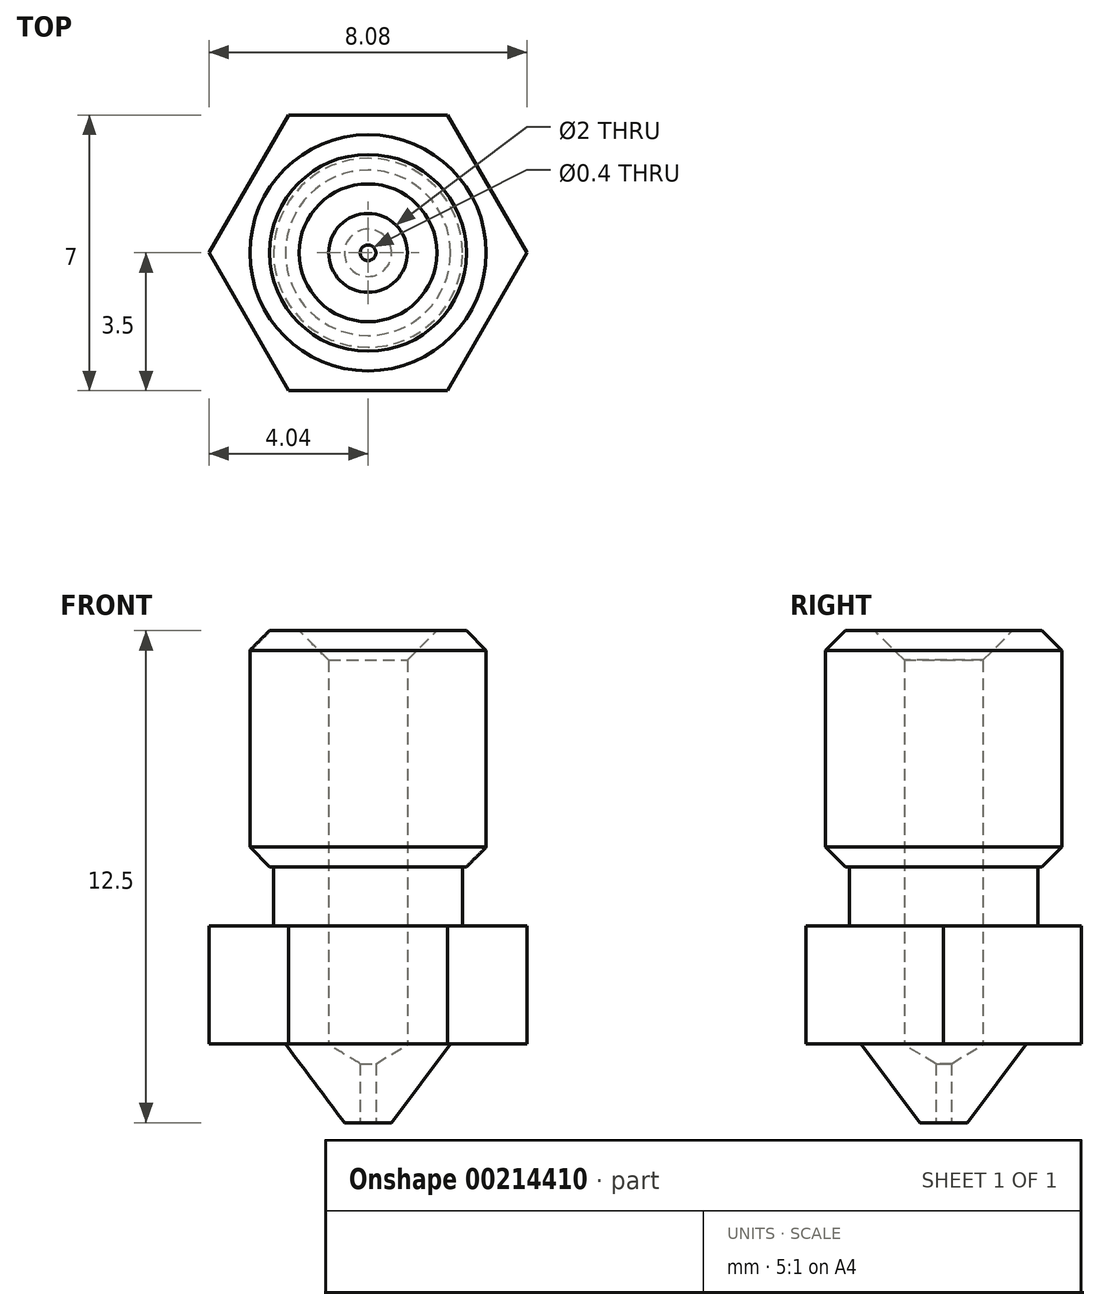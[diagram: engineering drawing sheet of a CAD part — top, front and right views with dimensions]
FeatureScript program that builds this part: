
annotation { "Feature Type Name" : "Feature", "Feature Type Description" : "" }
export const myFeature = defineFeature(function(context is Context, id is Id, definition is map)
    precondition{}
    {
        {
            var Q0;
            Q0=qCreatedBy(makeId("Front.planeOp"),FACE);
            var sketch = newSketch(context, id + "F0", { "sketchPlane" : qUnion([Q0])});
            skLineSegment(sketch, "E0", {"start": v(0, 0) * mm, "end": v(0, 12.5) * mm, "construction": true});
            skLineSegment(sketch, "E1", {"start": v(0.2, 0) * mm, "end": v(0.2, 1.5) * mm});
            skLineSegment(sketch, "E2", {"start": v(0.2, 0) * mm, "end": v(0.6, 0) * mm});
            skLineSegment(sketch, "E3", {"start": v(0.6, 0) * mm, "end": v(2.1, 2) * mm});
            skLineSegment(sketch, "E4", {"start": v(2.1, 2) * mm, "end": v(4.2, 2) * mm});
            skLineSegment(sketch, "E5", {"start": v(4.2, 2) * mm, "end": v(4.2, 5) * mm});
            skLineSegment(sketch, "E6", {"start": v(1, 12.5) * mm, "end": v(1, 1.98) * mm});
            skLineSegment(sketch, "E7", {"start": v(1, 1.98) * mm, "end": v(0.2, 1.5) * mm});
            skLineSegment(sketch, "E8", {"start": v(1, 12.5) * mm, "end": v(3, 12.5) * mm});
            skLineSegment(sketch, "E9", {"start": v(3, 12.5) * mm, "end": v(3, 6.5) * mm});
            skLineSegment(sketch, "E10", {"start": v(3, 6.5) * mm, "end": v(2.4, 6.5) * mm});
            skLineSegment(sketch, "E11", {"start": v(2.4, 6.5) * mm, "end": v(2.4, 5) * mm});
            skLineSegment(sketch, "E12", {"start": v(2.4, 5) * mm, "end": v(4.2, 5) * mm});
            skSolve(sketch);
        }
        {
            var Q0;
            Q0 = qSketchRegion(id + "F0", true);
            var Q1;
            Q1=sQuery(id+"F0.wireOp",EDGE,"E0");
            revolve(context, id + "F1", {"entities" : qUnion([Q0]), "axis" : qUnion([Q1]), "revolveType" : RevolveType.FULL});
        }
        {
            var Q0;
            Q0=makeQuery(id+"F1.opRevolve","SWEPT_EDGE",EDGE,{"disambiguationData":[OSD([sQuery(id+"F0.wireOp",EDGE,"E9"),sQuery(id+"F0.wireOp",EDGE,"E10")])]});
            var Q1;
            Q1=makeQuery(id+"F1.opRevolve","SWEPT_EDGE",EDGE,{"disambiguationData":[OSD([sQuery(id+"F0.wireOp",EDGE,"E8"),sQuery(id+"F0.wireOp",EDGE,"E9")])]});
            chamfer(context, id + "F2", {"entities" : qUnion([Q0, Q1]), "width" : 0.5 * mm, "tangentPropagation" : true});
        }
        {
            var Q0;
            Q0=makeQuery(id+"F1.opRevolve","SWEPT_EDGE",EDGE,{"disambiguationData":[OSD([sQuery(id+"F0.wireOp",EDGE,"E6"),sQuery(id+"F0.wireOp",EDGE,"E8")])]});
            chamfer(context, id + "F3", {"entities" : qUnion([Q0]), "width" : 0.75 * mm, "tangentPropagation" : true});
        }
        {
            var Q0;
            Q0=makeQuery(id+"F1.opRevolve","SWEPT_FACE",FACE,{"disambiguationData":[OSD([sQuery(id+"F0.wireOp",EDGE,"E4")])]});
            var sketch = newSketch(context, id + "F4", { "sketchPlane" : qUnion([Q0])});
            skCircle(sketch, "E13.cCircle", {"center": v(0, 0) * mm, "radius": 3.5 * mm, "construction": true});
            skLineSegment(sketch, "E13.0", {"start": v(-2.02, -3.5) * mm, "end": v(-4.04, 0) * mm});
            skLineSegment(sketch, "E13.1", {"start": v(-4.04, 0) * mm, "end": v(-2.02, 3.5) * mm});
            skLineSegment(sketch, "E13.2", {"start": v(-2.02, 3.5) * mm, "end": v(2.02, 3.5) * mm});
            skLineSegment(sketch, "E13.3", {"start": v(2.02, 3.5) * mm, "end": v(4.04, 0) * mm});
            skLineSegment(sketch, "E13.4", {"start": v(4.04, 0) * mm, "end": v(2.02, -3.5) * mm});
            skLineSegment(sketch, "E13.5", {"start": v(2.02, -3.5) * mm, "end": v(-2.02, -3.5) * mm});
            skPoint(sketch, "E13.0.midPoint", {"position": v(-3.03, -1.75) * mm});
            skLineSegment(sketch, "E14", {"start": v(-4.04, 0) * mm, "end": v(0, 0) * mm, "construction": true});
            skCircle(sketch, "E15", {"center": v(0, 0) * mm, "radius": 5 * mm});
            skSolve(sketch);
        }
        {
            var Q0;
            Q0 = qSketchRegion(id + "F4", true);
            extrude(context, id + "F5", {"entities" : qUnion([Q0]), "operationType" : NewBodyOperationType.REMOVE, "endBound" : BoundingType.THROUGH_ALL, "oppositeDirection" : true, "depth" : 25 * mm});
        }
    });
